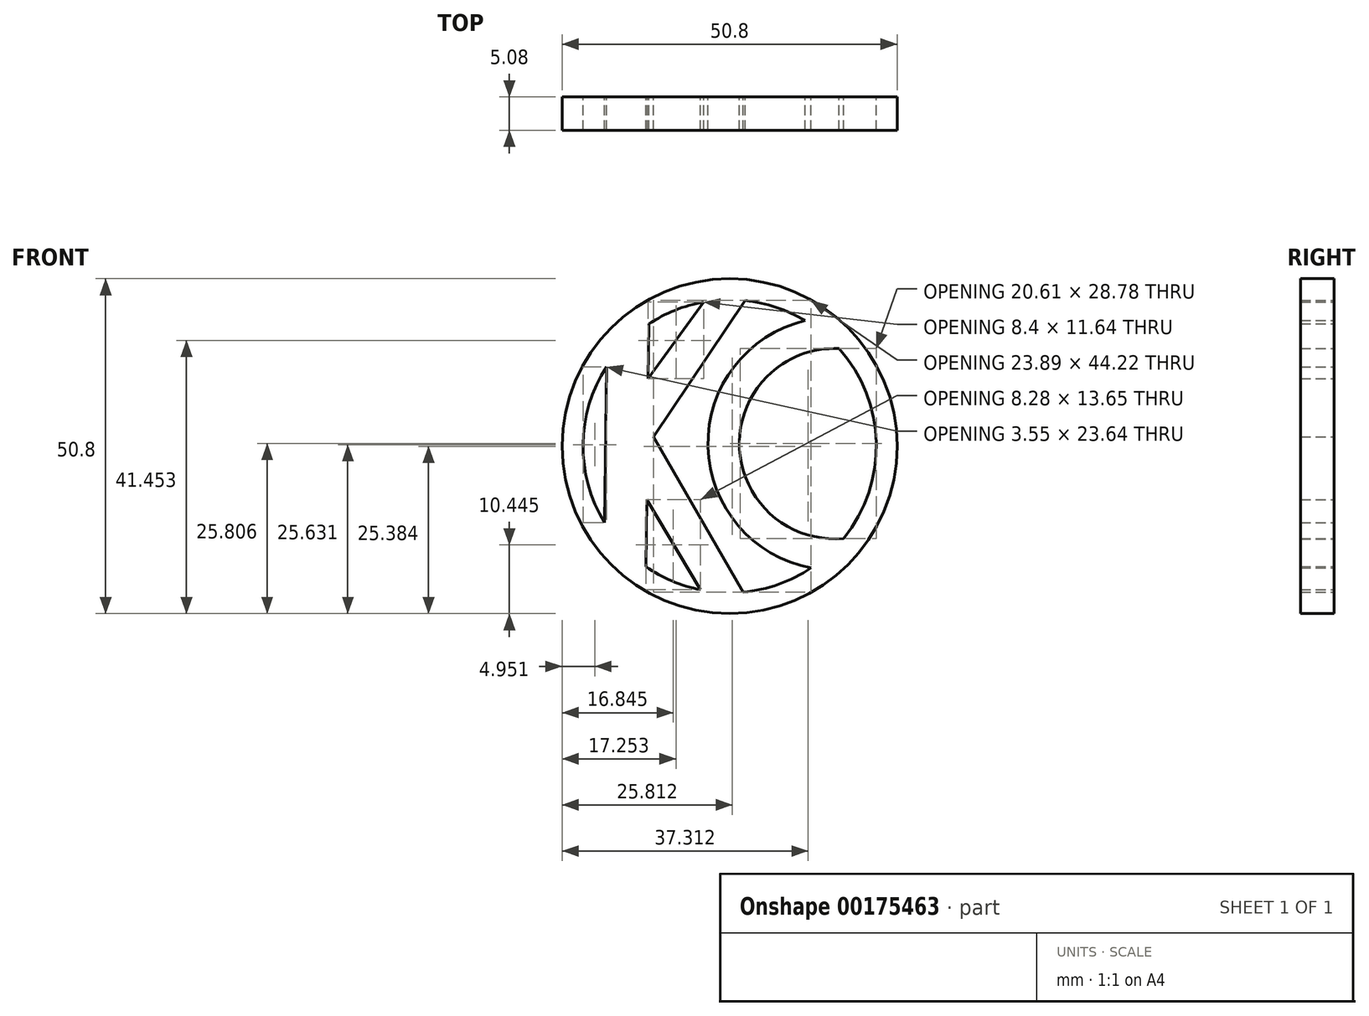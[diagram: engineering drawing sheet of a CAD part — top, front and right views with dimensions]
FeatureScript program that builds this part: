
annotation { "Feature Type Name" : "Feature", "Feature Type Description" : "" }
export const myFeature = defineFeature(function(context is Context, id is Id, definition is map)
    precondition{}
    {
        {
            var Q0;
            Q0=qCreatedBy(makeId("Front.planeOp"),FACE);
            var sketch = newSketch(context, id + "F0", { "sketchPlane" : qUnion([Q0])});
            skCircle(sketch, "E0", {"center": v(0, 0) * mm, "radius": 25.4 * mm});
            skArc(sketch, "E1", {"start": v(-18.67, 12.05) * mm, "mid": v(-22.22, 0.27) * mm, "end": v(-18.96, -11.59) * mm});
            skLineSegment(sketch, "E2.left", {"start": v(-18.67, 12.05) * mm, "end": v(-18.96, -11.59) * mm});
            skLineSegment(sketch, "E2.right", {"start": v(-12.24, 18.54) * mm, "end": v(-12.35, 10.23) * mm});
            skLineSegment(sketch, "E3", {"start": v(0, 18.54) * mm, "end": v(-11.53, 1.4) * mm});
            skPoint(sketch, "E4.endSnap0", {"position": v(-6.27, 6.71) * mm});
            skLineSegment(sketch, "E5.trimOffspring", {"start": v(-12.57, -8.13) * mm, "end": v(-12.7, -18.54) * mm});
            skPoint(sketch, "E6.orphan", {"position": v(-0.06, 13.43) * mm});
            skPoint(sketch, "E7.orphan", {"position": v(0, -12.6) * mm});
            skPoint(sketch, "E8.orphan", {"position": v(0, -18.54) * mm});
            skLineSegment(sketch, "E9", {"start": v(-12.24, 18.54) * mm, "end": v(-12.24, 18.55) * mm});
            skLineSegment(sketch, "E10", {"start": v(-12.7, -18.24) * mm, "end": v(-12.7, -18.54) * mm});
            skArc(sketch, "E11.trimOffspring", {"start": v(-12.7, -18.24) * mm, "mid": v(-8.74, -20.44) * mm, "end": v(-4.41, -21.78) * mm});
            skLineSegment(sketch, "E12", {"start": v(-6.35, 18.54) * mm, "end": v(-12.35, 10.23) * mm});
            skPoint(sketch, "E13.orphan", {"position": v(-12.39, 6.71) * mm});
            skLineSegment(sketch, "E14", {"start": v(0, -18.54) * mm, "end": v(-11.53, 1.4) * mm});
            skLineSegment(sketch, "E15", {"start": v(-12.57, -8.13) * mm, "end": v(-6.35, -18.54) * mm});
            skPoint(sketch, "E16.orphan", {"position": v(-12.47, 0) * mm});
            skPoint(sketch, "E17.end.orphan", {"position": v(14.07, 6.71) * mm});
            skArc(sketch, "E18.trimOffspring", {"start": v(11.45, 19.05) * mm, "mid": v(7.08, 21.07) * mm, "end": v(2.4, 22.1) * mm});
            skArc(sketch, "E19.trimOffspring", {"start": v(17.27, -13.98) * mm, "mid": v(22.22, 0.53) * mm, "end": v(16.58, 14.8) * mm});
            skLineSegment(sketch, "E20", {"start": v(-12.35, 10.23) * mm, "end": v(-3.95, 21.87) * mm});
            skLineSegment(sketch, "E21", {"start": v(-11.53, 1.4) * mm, "end": v(2.4, 22.1) * mm});
            skLineSegment(sketch, "E22", {"start": v(-12.57, -8.13) * mm, "end": v(-4.41, -21.78) * mm});
            skLineSegment(sketch, "E23", {"start": v(-11.53, 1.4) * mm, "end": v(2.07, -22.13) * mm});
            skArc(sketch, "E24", {"start": v(11.45, 19.05) * mm, "mid": v(-3.27, -0.08) * mm, "end": v(12.36, -18.47) * mm});
            skLineSegment(sketch, "E25", {"start": v(16.58, -14.8) * mm, "end": v(16.54, -14.85) * mm});
            skPoint(sketch, "E26.orphan", {"position": v(16.58, -19.24) * mm});
            skArc(sketch, "E27", {"start": v(-12.7, -18.32) * mm, "mid": v(-12.7, -18.32) * mm, "end": v(-12.7, -18.32) * mm});
            skArc(sketch, "E28", {"start": v(5.69, 10.58) * mm, "mid": v(2.85, -5.77) * mm, "end": v(17.27, -13.98) * mm});
            skArc(sketch, "E29.trimOffspring", {"start": v(2.07, -22.13) * mm, "mid": v(7.44, -20.94) * mm, "end": v(12.36, -18.47) * mm});
            skArc(sketch, "E30.trimOffspring", {"start": v(-3.95, 21.87) * mm, "mid": v(-8.26, 20.63) * mm, "end": v(-12.24, 18.55) * mm});
            skArc(sketch, "E31", {"start": v(16.58, 14.8) * mm, "mid": v(1.47, 0.04) * mm, "end": v(17.27, -13.98) * mm});
            skSolve(sketch);
        }
        {
            var Q0;
            Q0=makeQuery(id+"F0.imprint","IMPRINT",FACE,{"disambiguationData":[TD([[makeQuery(id+"F0.imprint","IMPRINT",EDGE,{"derivedFrom":sQuery(id+"F0.wireOp",EDGE,"E0")}),1.0]])]});
            var sketch = newSketch(context, id + "F1", { "sketchPlane" : qUnion([Q0])});
            skCircle(sketch, "E32", {"center": v(0, 0) * mm, "radius": 25.4 * mm});
            skSolve(sketch);
        }
        {
            var Q0;
            Q0 = qSketchRegion(id + "F1", true);
            extrude(context, id + "F2", {"entities" : qUnion([Q0]), "depth" : 5.08 * mm});
        }
        {
            var Q0;
            {var subQ4=sQuery(id+"F0.wireOp",EDGE,"E18.trimOffspring");Q0=makeQuery(id+"F0.imprint","IMPRINT",FACE,{"disambiguationData":[TD([[makeQuery(id+"F0.imprint","IMPRINT",EDGE,{"derivedFrom":subQ4}),1.0]])]});}
            var Q1;
            {var subQ0=sQuery(id+"F0.wireOp",EDGE,"E19.trimOffspring");Q1=makeQuery(id+"F0.imprint","IMPRINT",FACE,{"disambiguationData":[TD([[makeQuery(id+"F0.imprint","IMPRINT",EDGE,{"derivedFrom":subQ0}),1.0]])]});}
            var Q2;
            Q2=makeQuery(id+"F0.imprint","IMPRINT",FACE,{"disambiguationData":[TD([[makeQuery(id+"F0.imprint","IMPRINT",EDGE,{"derivedFrom":sQuery(id+"F0.wireOp",EDGE,"E1")}),1.0]])]});
            var Q3;
            {var subQ3=sQuery(id+"F0.wireOp",EDGE,"E2.right");Q3=makeQuery(id+"F0.imprint","IMPRINT",FACE,{"disambiguationData":[TD([[makeQuery(id+"F0.imprint","IMPRINT",EDGE,{"derivedFrom":subQ3}),1.0]])]});}
            var Q4;
            {var subQ0=sQuery(id+"F0.wireOp",EDGE,"E22");var subQ6=makeQuery(id+"F0.imprint","IMPRINT",VERTEX,{"derivedFrom":subQ0});Q4=makeQuery(id+"F0.imprint","IMPRINT",FACE,{"disambiguationData":[TD([[makeQuery(id+"F0.imprint","IMPRINT",EDGE,{"disambiguationData":[TD([[subQ6,1.0]])],"derivedFrom":subQ0}),-1.0]])]});}
            extrude(context, id + "F3", {"entities" : qUnion([Q0, Q1, Q2, Q3, Q4]), "operationType" : NewBodyOperationType.REMOVE, "depth" : 25.4 * mm});
        }
    });
